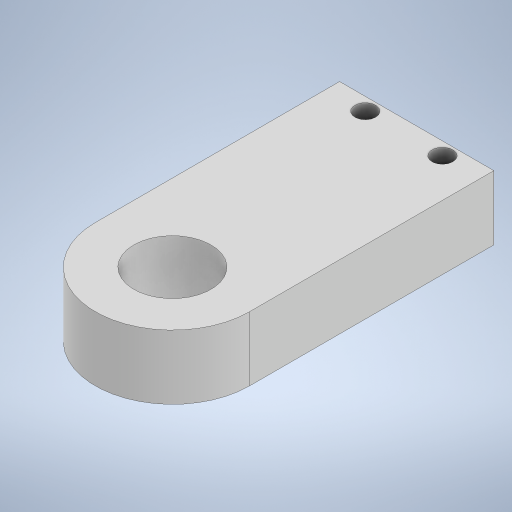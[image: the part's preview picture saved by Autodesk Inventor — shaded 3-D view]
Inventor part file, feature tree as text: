
AUTODESK INVENTOR PART (.ipt)
format: ipt  version: 2023.2 (Build 272271030, 271C)  size: 225,280 bytes
history: native  units: mm
features: extrude x2, sketch x2, projected_geometry x1
ambient origin geometry x8: Origin, YZ Plane, XZ Plane, XY Plane, X Axis, Y Axis, Z Axis, Center Point
bodies: Solid1 (feature_tree)
feature tree (5):
  extrude  "Extrusion1"  Depth=60.0mm
  extrude  "Extrusion2"  Depth=25.0mm TaperAngle=0.0deg
  sketch  "Sketch1"  dims[d0=60.0mm d1=95.0mm]
  sketch  "Sketch2"  dims[d2=30.0mm d3=25.0mm d4=0.0mm d5=10.0mm d6=8.1mm d7=30.0mm d8=0.0mm d9=0.0mm]
  projected_geometry  "Projected Loop1"
